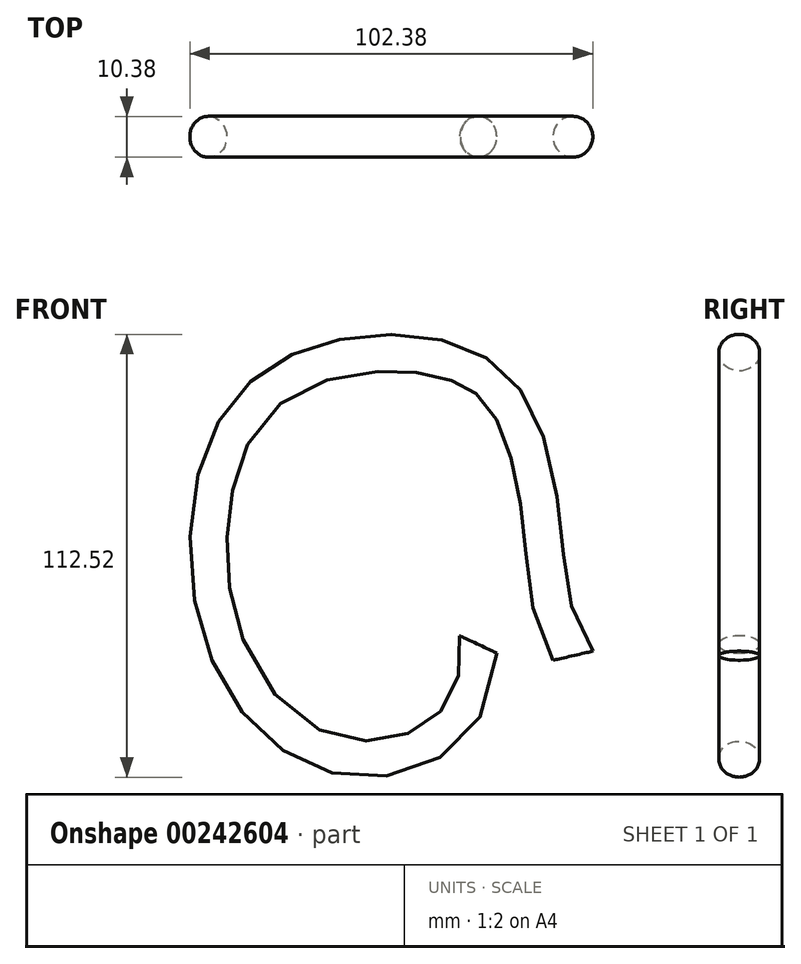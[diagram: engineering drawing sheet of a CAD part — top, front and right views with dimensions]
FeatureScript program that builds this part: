
annotation { "Feature Type Name" : "Feature", "Feature Type Description" : "" }
export const myFeature = defineFeature(function(context is Context, id is Id, definition is map)
    precondition{}
    {
        {
            var Q0;
            Q0=qCreatedBy(makeId("Front.planeOp"),FACE);
            var sketch = newSketch(context, id + "F0", { "sketchPlane" : qUnion([Q0])});
            skPoint(sketch, "E0.visualSharp", {"position": v(44.7, 0) * mm});
            skFitSpline(sketch, "E1", {"points": [v(60.12, -59.6) * mm, v(52.02, -28.27) * mm, v(38.29, 10.92) * mm, v(0, 20.5) * mm, v(-34.6, 0) * mm, v(-37.75, -60.4) * mm, v(0, -91.75) * mm, v(35.7, -60.2) * mm], "startDerivative": vector(-162.47, 217.53) * mm, "endDerivative": vector(7.5, 460.78) * mm});
            skSolve(sketch);
        }
        {
            var Q0;
            Q0=qCreatedBy(makeId("Top.planeOp"),FACE);
            var sketch = newSketch(context, id + "F1", { "sketchPlane" : qUnion([Q0])});
            skCircle(sketch, "E2", {"center": v(40.15, 0) * mm, "radius": 5.2 * mm});
            skSolve(sketch);
        }
        {
            var Q0;
            Q0=makeQuery(id+"F1.imprint","IMPRINT",FACE,{"disambiguationData":[TD([[makeQuery(id+"F1.imprint","IMPRINT",EDGE,{"derivedFrom":sQuery(id+"F1.wireOp",EDGE,"E2")}),1.0]])]});
            var Q1;
            Q1 = qConstructionFilter(qBodyType(qCreatedBy(id + "F0" ,EDGE), BodyType.WIRE), ConstructionObject.NO);
            sweep(context, id + "F2", {"profiles" : qUnion([Q0]), "path" : qUnion([Q1])});
        }
    });
